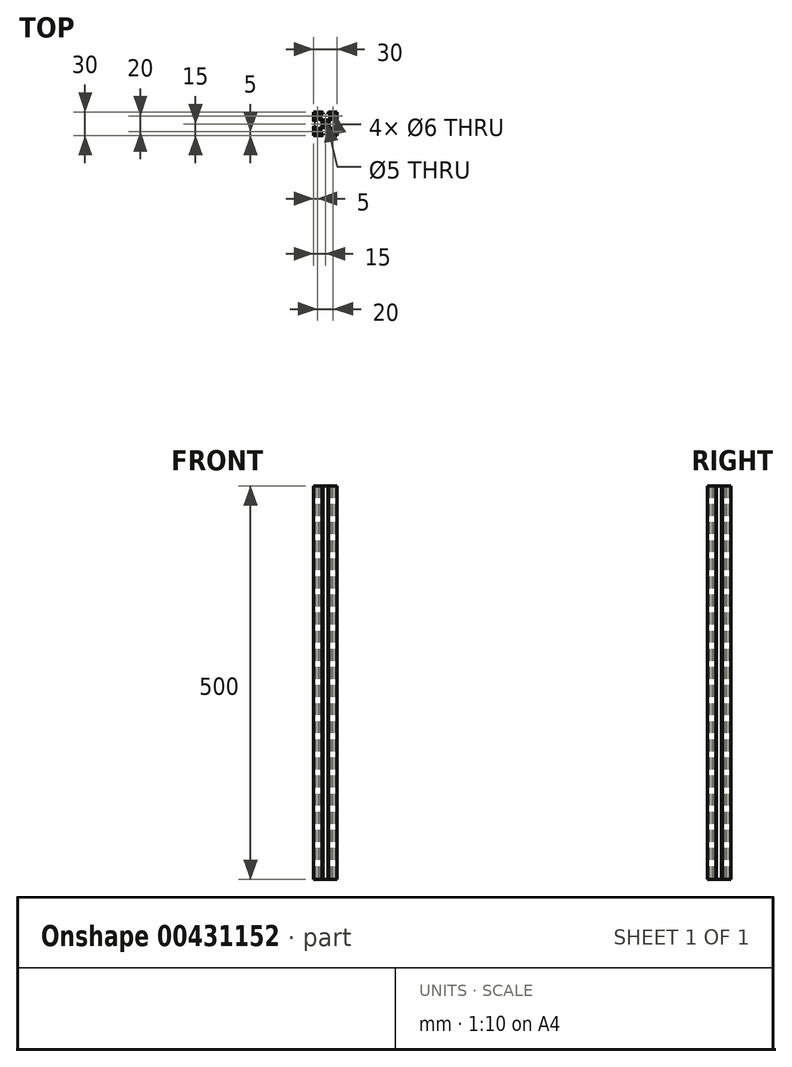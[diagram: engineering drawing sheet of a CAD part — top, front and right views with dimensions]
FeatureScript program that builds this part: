
annotation { "Feature Type Name" : "Feature", "Feature Type Description" : "" }
export const myFeature = defineFeature(function(context is Context, id is Id, definition is map)
    precondition{}
    {
        {
            var Q0;
            Q0=qCreatedBy(makeId("Top.planeOp"),FACE);
            var sketch = newSketch(context, id + "F0", { "sketchPlane" : qUnion([Q0])});
            skLineSegment(sketch, "E0.bottom", {"start": v(15, 15) * mm, "end": v(3.95, 15) * mm});
            skLineSegment(sketch, "E0.top", {"start": v(15, -15) * mm, "end": v(3.95, -15) * mm});
            skLineSegment(sketch, "E0.left", {"start": v(15, 15) * mm, "end": v(15, 3.95) * mm});
            skLineSegment(sketch, "E0.right", {"start": v(-15, 15) * mm, "end": v(-15, 3.95) * mm});
            skPoint(sketch, "E0.middle", {"position": v(0, 0) * mm});
            skLineSegment(sketch, "E1", {"start": v(0, 15) * mm, "end": v(0, -15) * mm, "construction": true});
            skLineSegment(sketch, "E2", {"start": v(-15, 0) * mm, "end": v(15, 0) * mm, "construction": true});
            skCircle(sketch, "E3", {"center": v(-10, 10) * mm, "radius": 3 * mm});
            skCircle(sketch, "E4", {"center": v(0, 0) * mm, "radius": 2.5 * mm});
            skLineSegment(sketch, "E5", {"start": v(0, 15) * mm, "end": v(0, 12.5) * mm, "construction": true});
            skLineSegment(sketch, "E6", {"start": v(-3.15, 14.5) * mm, "end": v(-3.15, 12.5) * mm});
            skLineSegment(sketch, "E7", {"start": v(-3.15, 12.5) * mm, "end": v(-5.1, 12.5) * mm});
            skLineSegment(sketch, "E8", {"start": v(0, 0) * mm, "end": v(-3.44, 0) * mm, "construction": true});
            skLineSegment(sketch, "E9", {"start": v(-5.1, 12.5) * mm, "end": v(-6.18, 9.16) * mm});
            skLineSegment(sketch, "E10", {"start": v(-3.44, 4.5) * mm, "end": v(0, 4.5) * mm});
            skLineSegment(sketch, "E11", {"start": v(3.36, 15) * mm, "end": v(3.36, 11.64) * mm, "construction": true});
            skArc(sketch, "E12", {"start": v(-3.44, 4.5) * mm, "mid": v(-5.13, 6.64) * mm, "end": v(-6.18, 9.16) * mm});
            skLineSegment(sketch, "E13", {"start": v(-3.95, 15) * mm, "end": v(-3.15, 14.5) * mm});
            skLineSegment(sketch, "E14.trimOffspring", {"start": v(-3.95, 15) * mm, "end": v(-5.1, 15) * mm, "construction": true});
            skLineSegment(sketch, "E15", {"start": v(-15, 15) * mm, "end": v(15, -15) * mm, "construction": true});
            skLineSegment(sketch, "E16", {"start": v(15, 15) * mm, "end": v(-15, -15) * mm, "construction": true});
            skArc(sketch, "E17.MirrorCS", {"start": v(-4.5, 3.43) * mm, "mid": v(-6.64, 5.13) * mm, "end": v(-9.16, 6.18) * mm});
            skLineSegment(sketch, "E18.MirrorCS", {"start": v(-4.5, 3.43) * mm, "end": v(-4.5, 0) * mm});
            skLineSegment(sketch, "E19.MirrorCS", {"start": v(-12.5, 5.1) * mm, "end": v(-9.16, 6.18) * mm});
            skLineSegment(sketch, "E20.MirrorCS", {"start": v(-12.5, 3.15) * mm, "end": v(-12.5, 5.1) * mm});
            skLineSegment(sketch, "E21.MirrorCS", {"start": v(-15, 3.95) * mm, "end": v(-14.5, 3.15) * mm});
            skLineSegment(sketch, "E22.MirrorCS", {"start": v(-14.5, 3.15) * mm, "end": v(-12.5, 3.15) * mm});
            skLineSegment(sketch, "E23.MirrorCS", {"start": v(-14.5, -3.15) * mm, "end": v(-12.5, -3.15) * mm});
            skLineSegment(sketch, "E24.MirrorCS", {"start": v(-15, -3.95) * mm, "end": v(-14.5, -3.15) * mm});
            skLineSegment(sketch, "E25.MirrorCS", {"start": v(-12.5, -3.15) * mm, "end": v(-12.5, -5.1) * mm});
            skLineSegment(sketch, "E26.MirrorCS", {"start": v(-12.5, -5.1) * mm, "end": v(-9.16, -6.18) * mm});
            skArc(sketch, "E27.MirrorCS", {"start": v(-4.5, -3.43) * mm, "mid": v(-6.64, -5.13) * mm, "end": v(-9.16, -6.18) * mm});
            skLineSegment(sketch, "E28.MirrorCS", {"start": v(-4.5, -3.43) * mm, "end": v(-4.5, 0) * mm});
            skLineSegment(sketch, "E29.MirrorCS", {"start": v(-3.44, -4.5) * mm, "end": v(0, -4.5) * mm});
            skArc(sketch, "E30.MirrorCS", {"start": v(-3.44, -4.5) * mm, "mid": v(-5.13, -6.64) * mm, "end": v(-6.18, -9.16) * mm});
            skLineSegment(sketch, "E31.MirrorCS", {"start": v(-5.1, -12.5) * mm, "end": v(-6.18, -9.16) * mm});
            skLineSegment(sketch, "E32.MirrorCS", {"start": v(-3.15, -12.5) * mm, "end": v(-5.1, -12.5) * mm});
            skLineSegment(sketch, "E33.MirrorCS", {"start": v(-3.95, -15) * mm, "end": v(-3.15, -14.5) * mm});
            skLineSegment(sketch, "E34.MirrorCS", {"start": v(-3.15, -14.5) * mm, "end": v(-3.15, -12.5) * mm});
            skLineSegment(sketch, "E35.MirrorCS", {"start": v(3.44, -4.5) * mm, "end": v(0, -4.5) * mm});
            skArc(sketch, "E36.MirrorCS", {"start": v(3.44, -4.5) * mm, "mid": v(5.13, -6.64) * mm, "end": v(6.18, -9.16) * mm});
            skLineSegment(sketch, "E37.MirrorCS", {"start": v(5.1, -12.5) * mm, "end": v(6.18, -9.16) * mm});
            skLineSegment(sketch, "E38.MirrorCS", {"start": v(3.15, -12.5) * mm, "end": v(5.1, -12.5) * mm});
            skLineSegment(sketch, "E39.MirrorCS", {"start": v(3.15, -14.5) * mm, "end": v(3.15, -12.5) * mm});
            skLineSegment(sketch, "E40.MirrorCS", {"start": v(3.95, -15) * mm, "end": v(3.15, -14.5) * mm});
            skArc(sketch, "E41.MirrorCS", {"start": v(4.5, -3.43) * mm, "mid": v(6.64, -5.13) * mm, "end": v(9.16, -6.18) * mm});
            skLineSegment(sketch, "E42.MirrorCS", {"start": v(4.5, 3.44) * mm, "end": v(4.5, 0) * mm});
            skLineSegment(sketch, "E43.MirrorCS", {"start": v(4.5, -3.43) * mm, "end": v(4.5, 0) * mm});
            skArc(sketch, "E44.MirrorCS", {"start": v(4.5, 3.44) * mm, "mid": v(6.64, 5.13) * mm, "end": v(9.16, 6.18) * mm});
            skLineSegment(sketch, "E45.MirrorCS", {"start": v(12.5, 5.1) * mm, "end": v(9.16, 6.18) * mm});
            skLineSegment(sketch, "E46.MirrorCS", {"start": v(12.5, -5.1) * mm, "end": v(9.16, -6.18) * mm});
            skLineSegment(sketch, "E47.MirrorCS", {"start": v(12.5, -3.15) * mm, "end": v(12.5, -5.1) * mm});
            skLineSegment(sketch, "E48.MirrorCS", {"start": v(14.5, -3.15) * mm, "end": v(12.5, -3.15) * mm});
            skLineSegment(sketch, "E49.MirrorCS", {"start": v(12.5, 3.15) * mm, "end": v(12.5, 5.1) * mm});
            skLineSegment(sketch, "E50.MirrorCS", {"start": v(14.5, 3.15) * mm, "end": v(12.5, 3.15) * mm});
            skLineSegment(sketch, "E51.MirrorCS", {"start": v(15, 3.95) * mm, "end": v(14.5, 3.15) * mm});
            skLineSegment(sketch, "E52.MirrorCS", {"start": v(15, -3.95) * mm, "end": v(14.5, -3.15) * mm});
            skLineSegment(sketch, "E53.MirrorCS", {"start": v(3.43, 4.5) * mm, "end": v(0, 4.5) * mm});
            skArc(sketch, "E54.MirrorCS", {"start": v(3.43, 4.5) * mm, "mid": v(5.13, 6.64) * mm, "end": v(6.18, 9.16) * mm});
            skLineSegment(sketch, "E55.MirrorCS", {"start": v(5.1, 12.5) * mm, "end": v(6.18, 9.16) * mm});
            skLineSegment(sketch, "E56.MirrorCS", {"start": v(3.15, 12.5) * mm, "end": v(5.1, 12.5) * mm});
            skLineSegment(sketch, "E57.MirrorCS", {"start": v(3.15, 14.5) * mm, "end": v(3.15, 12.5) * mm});
            skLineSegment(sketch, "E58.MirrorCS", {"start": v(3.95, 15) * mm, "end": v(3.15, 14.5) * mm});
            skCircle(sketch, "E59.MirrorC", {"center": v(10, 10) * mm, "radius": 3 * mm});
            skCircle(sketch, "E60.MirrorC", {"center": v(10, -10) * mm, "radius": 3 * mm});
            skCircle(sketch, "E61.MirrorC", {"center": v(-10, -10) * mm, "radius": 3 * mm});
            skLineSegment(sketch, "E62.trimOffspring", {"start": v(-15, -3.95) * mm, "end": v(-15, -15) * mm});
            skPoint(sketch, "E63.orphan", {"position": v(-15, 3.15) * mm});
            skPoint(sketch, "E64.orphan", {"position": v(-15, -3.15) * mm});
            skLineSegment(sketch, "E65.trimOffspring", {"start": v(-3.95, -15) * mm, "end": v(-15, -15) * mm});
            skPoint(sketch, "E66.orphan", {"position": v(-3.15, -15) * mm});
            skPoint(sketch, "E67.orphan", {"position": v(3.15, -15) * mm});
            skLineSegment(sketch, "E68.trimOffspring", {"start": v(15, -3.95) * mm, "end": v(15, -15) * mm});
            skPoint(sketch, "E69.orphan", {"position": v(15, 3.15) * mm});
            skPoint(sketch, "E70.orphan", {"position": v(15, -3.15) * mm});
            skPoint(sketch, "E71.trimOffspring.end.orphan", {"position": v(3.15, 15) * mm});
            skLineSegment(sketch, "E72.trimOffspring", {"start": v(-3.95, 15) * mm, "end": v(-15, 15) * mm});
            skPoint(sketch, "E73.trimOffspring.end.orphan", {"position": v(-3.15, 15) * mm});
            skSolve(sketch);
        }
        {
            var Q0;
            Q0=makeQuery(id+"F0.imprint","IMPRINT",FACE,{"disambiguationData":[TD([[makeQuery(id+"F0.imprint","IMPRINT",EDGE,{"derivedFrom":sQuery(id+"F0.wireOp",EDGE,"E0.bottom")}),1.0]])]});
            extrude(context, id + "F1", {"entities" : qUnion([Q0]), "endBound" : BoundingType.SYMMETRIC, "depth" : 500 * mm});
        }
    });
